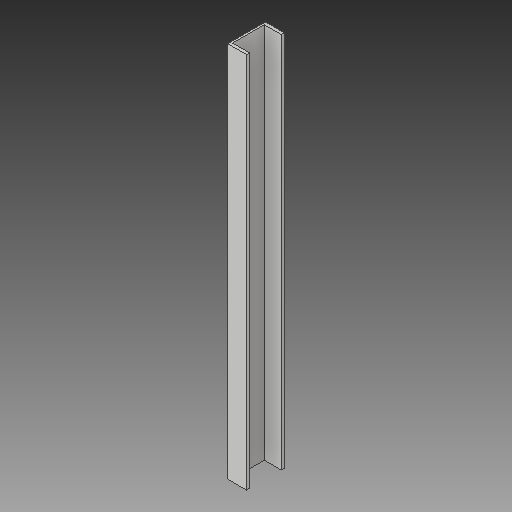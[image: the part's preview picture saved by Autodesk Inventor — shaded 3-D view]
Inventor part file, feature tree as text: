
AUTODESK INVENTOR PART (.ipt)
format: ipt  version: 2019 (Build 230136000, 136)  size: 90,624 bytes
history: native  units: in
note: dims shown in document units (in); Inventor stores cm internally (conversion verified against a paired STEP export)
features: other x3, sketch x1
ambient origin geometry x8: Origin, YZ Plane, XZ Plane, XY Plane, X Axis, Y Axis, Z Axis, Center Point
bodies: Solid1 (feature_tree)
feature tree (4):
  other  "Channel1_MIR3.ipt"
  other  "Solid1::Channel1_MIR3.ipt"
  other  "TaggingFeature1"
  sketch  "Sketch1"  dims[d0=0.3937in]
